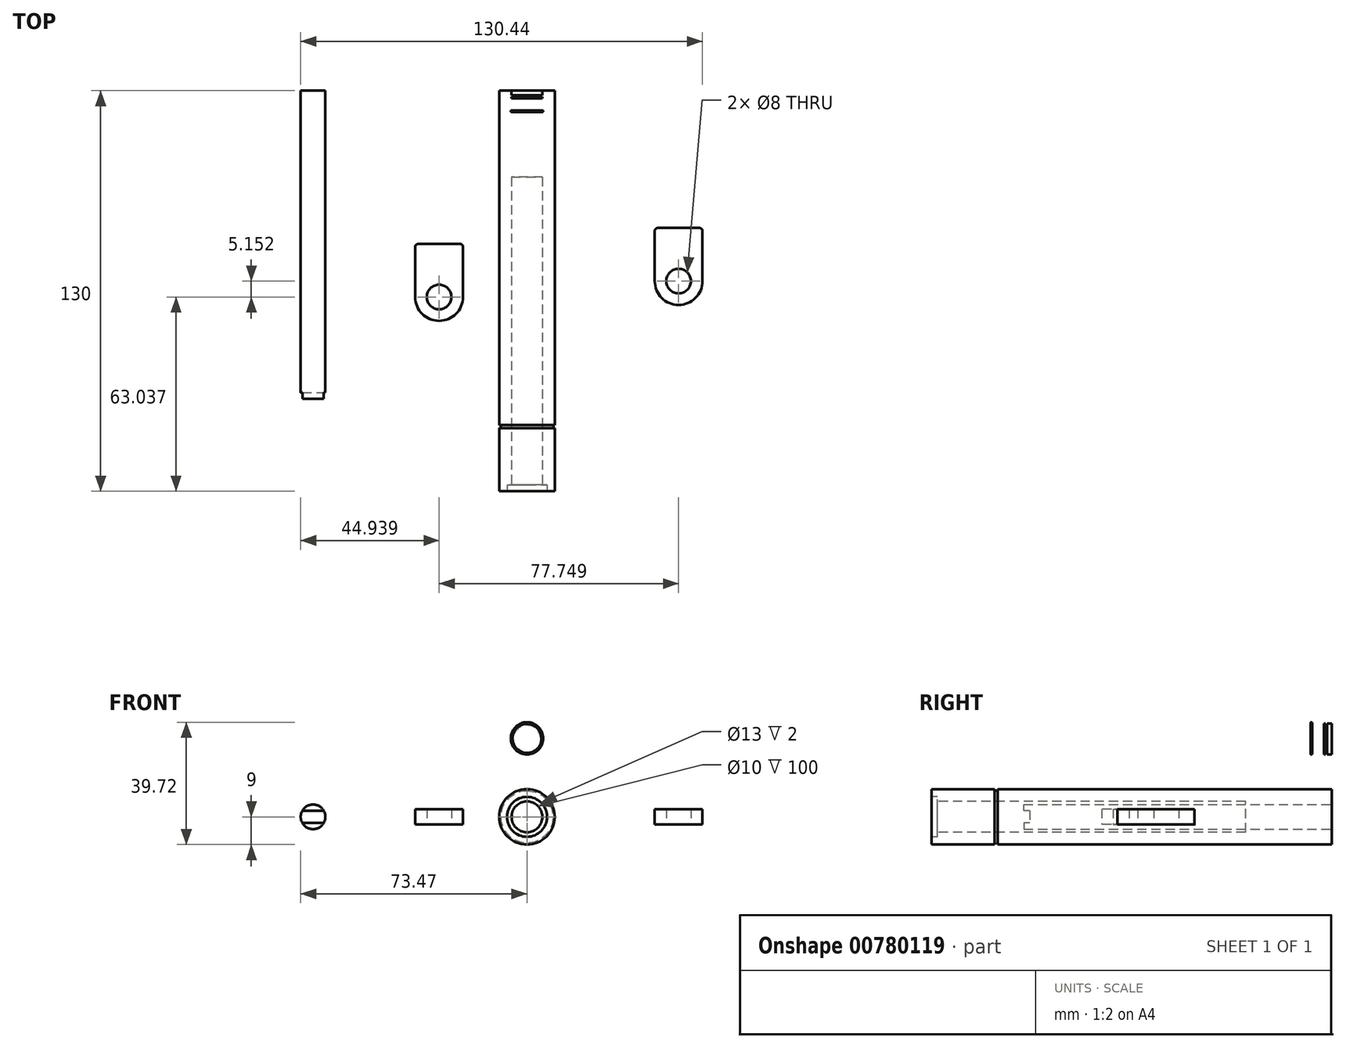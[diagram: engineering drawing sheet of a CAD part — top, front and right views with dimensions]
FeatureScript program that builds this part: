
annotation { "Feature Type Name" : "Feature", "Feature Type Description" : "" }
export const myFeature = defineFeature(function(context is Context, id is Id, definition is map)
    precondition{}
    {
        {
            var Q0;
            Q0=qCreatedBy(makeId("Front.planeOp"),FACE);
            var sketch = newSketch(context, id + "F0", { "sketchPlane" : qUnion([Q0])});
            skCircle(sketch, "E0", {"center": v(-69.47, 0) * mm, "radius": 4 * mm});
            skSolve(sketch);
        }
        {
            var Q0;
            Q0 = qSketchRegion(id + "F0", true);
            extrude(context, id + "F1", {"entities" : qUnion([Q0]), "depth" : 100 * mm, "offsetDistance" : 25 * mm});
        }
        {
            var Q0;
            Q0=qCreatedBy(makeId("Front.planeOp"),FACE);
            var sketch = newSketch(context, id + "F2", { "sketchPlane" : qUnion([Q0])});
            skCircle(sketch, "E1", {"center": v(0, 0) * mm, "radius": 9 * mm});
            skSolve(sketch);
        }
        {
            var Q0;
            Q0 = qSketchRegion(id + "F2", true);
            extrude(context, id + "F3", {"entities" : qUnion([Q0]), "depth" : 130 * mm, "offsetDistance" : 25 * mm});
        }
        {
            var Q0;
            Q0=qCreatedBy(makeId("Top.planeOp"),FACE);
            var sketch = newSketch(context, id + "F4", { "sketchPlane" : qUnion([Q0])});
            skCircle(sketch, "E2", {"center": v(-28.53, -66.96) * mm, "radius": 7.75 * mm});
            skLineSegment(sketch, "E3", {"start": v(-36.28, -66.96) * mm, "end": v(-36.28, -49.71) * mm});
            skLineSegment(sketch, "E4", {"start": v(-20.78, -66.96) * mm, "end": v(-20.78, -49.71) * mm});
            skLineSegment(sketch, "E5", {"start": v(-20.78, -49.71) * mm, "end": v(-36.28, -49.71) * mm});
            skCircle(sketch, "E6", {"center": v(-28.53, -66.96) * mm, "radius": 4 * mm});
            skLineSegment(sketch, "E7", {"start": v(-47.5, -99.97) * mm, "end": v(-63, -99.97) * mm});
            skCircle(sketch, "E8", {"center": v(49.22, -61.81) * mm, "radius": 7.75 * mm});
            skLineSegment(sketch, "E9", {"start": v(41.47, -61.81) * mm, "end": v(41.47, -44.56) * mm});
            skLineSegment(sketch, "E10", {"start": v(56.97, -61.81) * mm, "end": v(56.97, -44.56) * mm});
            skLineSegment(sketch, "E11", {"start": v(56.97, -44.56) * mm, "end": v(41.47, -44.56) * mm});
            skCircle(sketch, "E12", {"center": v(49.22, -61.81) * mm, "radius": 4 * mm});
            skSolve(sketch);
        }
        {
            var Q0;
            Q0 = qSketchRegion(id + "F4", true);
            extrude(context, id + "F5", {"entities" : qUnion([Q0]), "endBound" : BoundingType.SYMMETRIC, "depth" : 5 * mm, "offsetDistance" : 25 * mm});
        }
        {
            var Q0;
            Q0=makeQuery(id+"F5.opExtrude","SWEPT_EDGE",EDGE,{"disambiguationData":[OSD([sQuery(id+"F4.wireOp",EDGE,"E4"),sQuery(id+"F4.wireOp",EDGE,"E5")])]});
            var Q1;
            Q1=makeQuery(id+"F5.opExtrude","SWEPT_EDGE",EDGE,{"disambiguationData":[OSD([sQuery(id+"F4.wireOp",EDGE,"E3"),sQuery(id+"F4.wireOp",EDGE,"E5")])]});
            fillet(context, id + "F6", {"entities" : qUnion([Q0, Q1]), "radius" : 1 * mm, "tangentPropagation" : true, "allowEdgeOverflow" : false});
        }
        {
            var Q0;
            Q0=makeQuery(id+"F5.opExtrude","SWEPT_EDGE",EDGE,{"disambiguationData":[OSD([sQuery(id+"F4.wireOp",EDGE,"E9"),sQuery(id+"F4.wireOp",EDGE,"E11")])]});
            var Q1;
            Q1=makeQuery(id+"F5.opExtrude","SWEPT_EDGE",EDGE,{"disambiguationData":[OSD([sQuery(id+"F4.wireOp",EDGE,"E10"),sQuery(id+"F4.wireOp",EDGE,"E11")])]});
            fillet(context, id + "F7", {"entities" : qUnion([Q0, Q1]), "radius" : 1 * mm, "tangentPropagation" : true, "allowEdgeOverflow" : false});
        }
        {
            var Q0;
            Q0=qCreatedBy(makeId("Right.planeOp"),FACE);
            var sketch = newSketch(context, id + "F8", { "sketchPlane" : qUnion([Q0])});
            skCircle(sketch, "E13", {"center": v(-109, 9) * mm, "radius": 0.5 * mm});
            skSolve(sketch);
        }
        {
            var Q0;
            Q0=makeQuery(id+"F8.imprint","IMPRINT",FACE,{"disambiguationData":[TD([[makeQuery(id+"F8.imprint","IMPRINT",EDGE,{"derivedFrom":sQuery(id+"F8.wireOp",EDGE,"E13")}),1.0]])]});
            var Q1;
            Q1=sQuery(id+"F8.wireOp",EDGE,"E13");
            var Q2;
            Q2=makeQuery(id+"F3.opExtrude","SWEPT_FACE",FACE,{"disambiguationData":[OSD([sQuery(id+"F2.wireOp",EDGE,"E1")])]});
            revolve(context, id + "F9", {"operationType" : NewBodyOperationType.REMOVE, "surfaceOperationType" : NewSurfaceOperationType.NEW, "entities" : qUnion([Q0]), "surfaceEntities" : qUnion([Q1]), "axis" : qUnion([Q2]), "revolveType" : RevolveType.FULL, "oppositeDirection" : true});
        }
        {
            var Q0;
            Q0=makeQuery(id+"F1.opExtrude","CAP_FACE",FACE,{"disambiguationData":[OSD([sQuery(id+"F0.wireOp",EDGE,"E0")])],"isStart":false});
            var sketch = newSketch(context, id + "F10", { "sketchPlane" : qUnion([Q0])});
            skLineSegment(sketch, "E14.bottom", {"start": v(-72.93, 2) * mm, "end": v(-66, 2) * mm});
            skLineSegment(sketch, "E14.top", {"start": v(-72.93, -2) * mm, "end": v(-66, -2) * mm});
            skPoint(sketch, "E14.middle", {"position": v(-69.47, 0) * mm});
            skCircle(sketch, "E15.0.0", {"center": v(-69.47, 0) * mm, "radius": 4 * mm});
            skPoint(sketch, "E14.left.end.orphan", {"position": v(-78.54, -2) * mm});
            skPoint(sketch, "E14.left.start.orphan", {"position": v(-78.54, 2) * mm});
            skPoint(sketch, "E14.right.end.orphan", {"position": v(-60.4, -2) * mm});
            skPoint(sketch, "E14.right.start.orphan", {"position": v(-60.4, 2) * mm});
            skSolve(sketch);
        }
        {
            var Q0;
            {var subQ0=sQuery(id+"F10.wireOp",EDGE,"E14.bottom");Q0=makeQuery(id+"F10.imprint","IMPRINT",FACE,{"disambiguationData":[TD([[makeQuery(id+"F10.imprint","IMPRINT",EDGE,{"derivedFrom":subQ0}),-1.0]])]});}
            extrude(context, id + "F11", {"entities" : qUnion([Q0]), "operationType" : NewBodyOperationType.REMOVE, "oppositeDirection" : true, "depth" : 2 * mm, "offsetDistance" : 25 * mm});
        }
        {
            var Q0;
            Q0=makeQuery(id+"F3.opExtrude","CAP_FACE",FACE,{"disambiguationData":[OSD([sQuery(id+"F2.wireOp",EDGE,"E1")])],"isStart":false});
            var sketch = newSketch(context, id + "F12", { "sketchPlane" : qUnion([Q0])});
            skCircle(sketch, "E16", {"center": v(0, 0) * mm, "radius": 6.5 * mm});
            skSolve(sketch);
        }
        {
            var Q0;
            Q0 = qSketchRegion(id + "F12", true);
            extrude(context, id + "F13", {"entities" : qUnion([Q0]), "operationType" : NewBodyOperationType.REMOVE, "oppositeDirection" : true, "depth" : 2 * mm, "offsetDistance" : 25 * mm});
        }
        {
            var Q0;
            Q0=makeQuery(id+"F13.boolean.opBoolean","COPY",FACE,{"derivedFrom":makeQuery(id+"F13.opExtrude","CAP_FACE",FACE,{"disambiguationData":[OSD([sQuery(id+"F12.wireOp",EDGE,"E16")])],"isStart":false})});
            var sketch = newSketch(context, id + "F14", { "sketchPlane" : qUnion([Q0])});
            skCircle(sketch, "E17", {"center": v(0, 0) * mm, "radius": 5 * mm});
            skSolve(sketch);
        }
        {
            var Q0;
            Q0=makeQuery(id+"F14.imprint","IMPRINT",FACE,{"disambiguationData":[TD([[makeQuery(id+"F14.imprint","IMPRINT",EDGE,{"derivedFrom":sQuery(id+"F14.wireOp",EDGE,"E17")}),1.0]])]});
            extrude(context, id + "F15", {"entities" : qUnion([Q0]), "operationType" : NewBodyOperationType.REMOVE, "oppositeDirection" : true, "depth" : 100 * mm, "offsetDistance" : 25 * mm});
        }
        {
            var Q0;
            Q0=qCreatedBy(makeId("Right.planeOp"),FACE);
            var sketch = newSketch(context, id + "F16", { "sketchPlane" : qUnion([Q0])});
            skLineSegment(sketch, "E18", {"start": v(0, 25.24) * mm, "end": v(0, 30.24) * mm});
            skLineSegment(sketch, "E19", {"start": v(0, 30.24) * mm, "end": v(-1.5, 30.24) * mm});
            skLineSegment(sketch, "E20", {"start": v(-1.5, 30.24) * mm, "end": v(-1.5, 29.74) * mm});
            skLineSegment(sketch, "E21", {"start": v(-1.5, 29.74) * mm, "end": v(-2, 29.74) * mm});
            skLineSegment(sketch, "E22", {"start": v(-2, 29.74) * mm, "end": v(-2, 30.24) * mm});
            skLineSegment(sketch, "E23", {"start": v(-2, 30.24) * mm, "end": v(-2.5, 30.24) * mm});
            skLineSegment(sketch, "E24", {"start": v(-2.5, 30.24) * mm, "end": v(-2.5, 25.24) * mm});
            skLineSegment(sketch, "E25", {"start": v(-2.5, 25.24) * mm, "end": v(0, 25.24) * mm});
            skSolve(sketch);
        }
        {
            var Q0;
            Q0=makeQuery(id+"F16.imprint","IMPRINT",FACE,{"disambiguationData":[TD([[makeQuery(id+"F16.imprint","IMPRINT",EDGE,{"derivedFrom":sQuery(id+"F16.wireOp",EDGE,"E18")}),1.0]])]});
            var Q1;
            Q1=sQuery(id+"F16.wireOp",EDGE,"E25");
            revolve(context, id + "F17", {"surfaceOperationType" : NewSurfaceOperationType.NEW, "entities" : qUnion([Q0]), "axis" : qUnion([Q1]), "revolveType" : RevolveType.FULL});
        }
        {
            var Q0;
            Q0=qCreatedBy(makeId("Right.planeOp"),FACE);
            var sketch = newSketch(context, id + "F18", { "sketchPlane" : qUnion([Q0])});
            skCircle(sketch, "E26", {"center": v(-6.66, 30.47) * mm, "radius": 0.25 * mm});
            skLineSegment(sketch, "E27", {"start": v(-4.4, 25.47) * mm, "end": v(-10, 25.47) * mm});
            skSolve(sketch);
        }
        {
            var Q0;
            Q0 = qSketchRegion(id + "F18", true);
            var Q1;
            Q1=sQuery(id+"F18.wireOp",EDGE,"E27");
            revolve(context, id + "F19", {"surfaceOperationType" : NewSurfaceOperationType.NEW, "entities" : qUnion([Q0]), "axis" : qUnion([Q1]), "revolveType" : RevolveType.FULL});
        }
    });
